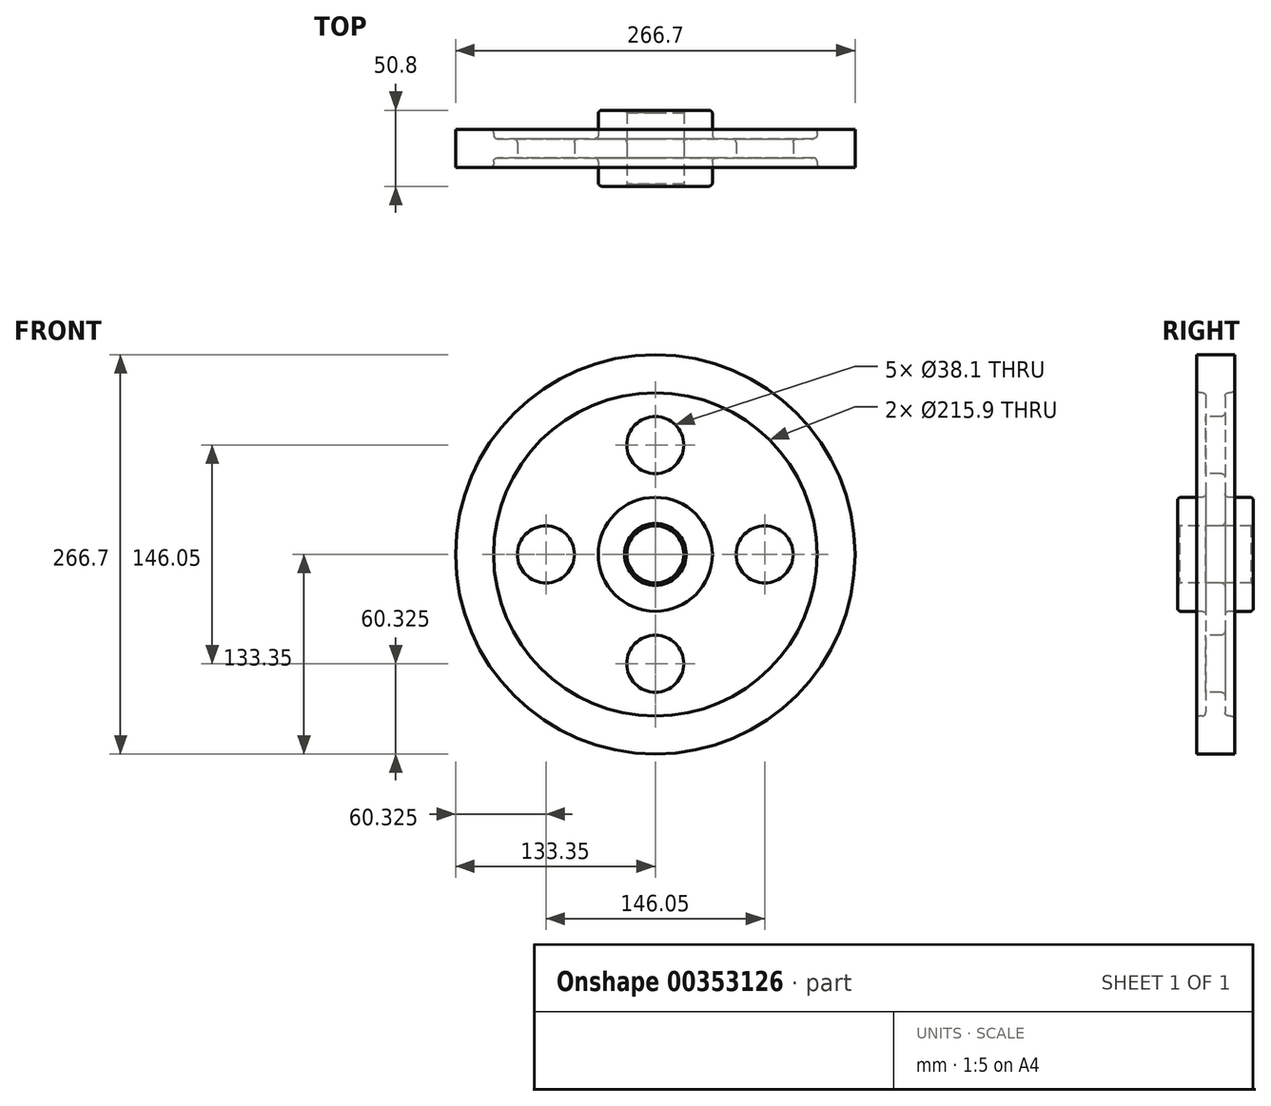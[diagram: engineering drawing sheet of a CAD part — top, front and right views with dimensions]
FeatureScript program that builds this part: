
annotation { "Feature Type Name" : "Feature", "Feature Type Description" : "" }
export const myFeature = defineFeature(function(context is Context, id is Id, definition is map)
    precondition{}
    {
        {
            var Q0;
            Q0=qCreatedBy(makeId("Right.planeOp"),FACE);
            var sketch = newSketch(context, id + "F0", { "sketchPlane" : qUnion([Q0])});
            skLineSegment(sketch, "E0", {"start": v(0, 0) * mm, "end": v(127.4, 0) * mm, "construction": true});
            skLineSegment(sketch, "E1.0", {"start": v(0, 19.05) * mm, "end": v(25.4, 19.05) * mm});
            skLineSegment(sketch, "E2.0", {"start": v(6.35, 38.1) * mm, "end": v(25.4, 38.1) * mm});
            skLineSegment(sketch, "E3.0", {"start": v(6.35, 107.95) * mm, "end": v(12.7, 107.95) * mm});
            skLineSegment(sketch, "E4.0", {"start": v(0, 133.35) * mm, "end": v(12.7, 133.35) * mm});
            skLineSegment(sketch, "E5", {"start": v(0, 133.35) * mm, "end": v(0, 0) * mm, "construction": true});
            skLineSegment(sketch, "E6.0", {"start": v(6.35, 107.95) * mm, "end": v(6.35, 38.1) * mm});
            skLineSegment(sketch, "E7.0", {"start": v(12.7, 133.35) * mm, "end": v(12.7, 107.95) * mm});
            skLineSegment(sketch, "E8.trimOffspring", {"start": v(25.4, 38.1) * mm, "end": v(25.4, 19.05) * mm});
            skLineSegment(sketch, "E9.MirrorCS", {"start": v(-6.35, 107.95) * mm, "end": v(-12.7, 107.95) * mm});
            skLineSegment(sketch, "E10.MirrorCS", {"start": v(-12.7, 133.35) * mm, "end": v(-12.7, 107.95) * mm});
            skLineSegment(sketch, "E11.MirrorCS", {"start": v(0, 133.35) * mm, "end": v(-12.7, 133.35) * mm});
            skLineSegment(sketch, "E12.MirrorCS", {"start": v(-6.35, 107.95) * mm, "end": v(-6.35, 38.1) * mm});
            skLineSegment(sketch, "E13.MirrorCS", {"start": v(-6.35, 38.1) * mm, "end": v(-25.4, 38.1) * mm});
            skLineSegment(sketch, "E14.MirrorCS", {"start": v(-25.4, 38.1) * mm, "end": v(-25.4, 19.05) * mm});
            skLineSegment(sketch, "E15.MirrorCS", {"start": v(0, 19.05) * mm, "end": v(-25.4, 19.05) * mm});
            skSolve(sketch);
        }
        {
            var Q0;
            Q0=makeQuery(id+"F0.imprint","IMPRINT",FACE,{"disambiguationData":[TD([[makeQuery(id+"F0.imprint","IMPRINT",EDGE,{"derivedFrom":sQuery(id+"F0.wireOp",EDGE,"E1.0")}),1.0]])]});
            var Q1;
            Q1=sQuery(id+"F0.wireOp",EDGE,"E0");
            revolve(context, id + "F1", {"entities" : qUnion([Q0]), "axis" : qUnion([Q1]), "revolveType" : RevolveType.FULL});
        }
        {
            var Q0;
            Q0=makeQuery(id+"F1.opRevolve","SWEPT_FACE",FACE,{"disambiguationData":[OSD([sQuery(id+"F0.wireOp",EDGE,"E12.MirrorCS")])]});
            var sketch = newSketch(context, id + "F2", { "sketchPlane" : qUnion([Q0])});
            skLineSegment(sketch, "E16", {"start": v(0, 0) * mm, "end": v(0, 73.03) * mm});
            skCircle(sketch, "E17", {"center": v(0, 73.03) * mm, "radius": 19.05 * mm});
            skCircle(sketch, "E18.1.0", {"center": v(-73.03, 0) * mm, "radius": 19.05 * mm});
            skCircle(sketch, "E18.2.0", {"center": v(0, -73.03) * mm, "radius": 19.05 * mm});
            skPoint(sketch, "E18.center", {"position": v(0, 0) * mm});
            skCircle(sketch, "E19.1.3.0", {"center": v(73.03, 0) * mm, "radius": 19.05 * mm});
            skSolve(sketch);
        }
        {
            var Q0;
            Q0=makeQuery(id+"F2.imprint","IMPRINT",FACE,{"disambiguationData":[TD([[makeQuery(id+"F2.imprint","IMPRINT",EDGE,{"derivedFrom":sQuery(id+"F2.wireOp",EDGE,"E17")}),1.0]])]});
            var Q1;
            Q1=makeQuery(id+"F2.imprint","IMPRINT",FACE,{"disambiguationData":[TD([[makeQuery(id+"F2.imprint","IMPRINT",EDGE,{"derivedFrom":sQuery(id+"F2.wireOp",EDGE,"E19.1.3.0")}),1.0]])]});
            var Q2;
            Q2=makeQuery(id+"F2.imprint","IMPRINT",FACE,{"disambiguationData":[TD([[makeQuery(id+"F2.imprint","IMPRINT",EDGE,{"derivedFrom":sQuery(id+"F2.wireOp",EDGE,"E18.2.0")}),1.0]])]});
            var Q3;
            Q3=makeQuery(id+"F2.imprint","IMPRINT",FACE,{"disambiguationData":[TD([[makeQuery(id+"F2.imprint","IMPRINT",EDGE,{"derivedFrom":sQuery(id+"F2.wireOp",EDGE,"E18.1.0")}),1.0]])]});
            extrude(context, id + "F3", {"entities" : qUnion([Q0, Q1, Q2, Q3]), "operationType" : NewBodyOperationType.REMOVE, "oppositeDirection" : true, "depth" : 25.4 * mm});
        }
        {
            var Q0;
            Q0=makeQuery(id+"F1.opRevolve","SWEPT_EDGE",EDGE,{"disambiguationData":[OSD([sQuery(id+"F0.wireOp",EDGE,"E9.MirrorCS"),sQuery(id+"F0.wireOp",EDGE,"E10.MirrorCS")])]});
            var Q1;
            Q1=makeQuery(id+"F1.opRevolve","SWEPT_EDGE",EDGE,{"disambiguationData":[OSD([sQuery(id+"F0.wireOp",EDGE,"E9.MirrorCS"),sQuery(id+"F0.wireOp",EDGE,"E12.MirrorCS")])]});
            var Q2;
            Q2=makeQuery(id+"F1.opRevolve","SWEPT_EDGE",EDGE,{"disambiguationData":[OSD([sQuery(id+"F0.wireOp",EDGE,"E12.MirrorCS"),sQuery(id+"F0.wireOp",EDGE,"E13.MirrorCS")])]});
            var Q3;
            Q3=makeQuery(id+"F1.opRevolve","SWEPT_EDGE",EDGE,{"disambiguationData":[OSD([sQuery(id+"F0.wireOp",EDGE,"E13.MirrorCS"),sQuery(id+"F0.wireOp",EDGE,"E14.MirrorCS")])]});
            var Q4;
            Q4=makeQuery(id+"F1.opRevolve","SWEPT_EDGE",EDGE,{"disambiguationData":[OSD([sQuery(id+"F0.wireOp",EDGE,"E3.0"),sQuery(id+"F0.wireOp",EDGE,"E7.0")])]});
            var Q5;
            Q5=makeQuery(id+"F1.opRevolve","SWEPT_FACE",FACE,{"disambiguationData":[OSD([sQuery(id+"F0.wireOp",EDGE,"E6.0")])]});
            var Q6;
            Q6=makeQuery(id+"F1.opRevolve","SWEPT_EDGE",EDGE,{"disambiguationData":[OSD([sQuery(id+"F0.wireOp",EDGE,"E2.0"),sQuery(id+"F0.wireOp",EDGE,"E8.trimOffspring")])]});
            var Q7;
            Q7=makeQuery(id+"F1.opRevolve","SWEPT_EDGE",EDGE,{"disambiguationData":[OSD([sQuery(id+"F0.wireOp",EDGE,"E2.0"),sQuery(id+"F0.wireOp",EDGE,"E6.0")])]});
            fillet(context, id + "F4", {"entities" : qUnion([Q0, Q1, Q2, Q3, Q4, Q5, Q6, Q7]), "radius" : 2.54 * mm, "tangentPropagation" : true, "allowEdgeOverflow" : false});
        }
        {
            var Q0;
            Q0=makeQuery(id+"F1.opRevolve","SWEPT_EDGE",EDGE,{"disambiguationData":[OSD([sQuery(id+"F0.wireOp",EDGE,"E1.0"),sQuery(id+"F0.wireOp",EDGE,"E8.trimOffspring")])]});
            var Q1;
            Q1=makeQuery(id+"F1.opRevolve","SWEPT_EDGE",EDGE,{"disambiguationData":[OSD([sQuery(id+"F0.wireOp",EDGE,"E14.MirrorCS"),sQuery(id+"F0.wireOp",EDGE,"E15.MirrorCS")])]});
            chamfer(context, id + "F5", {"entities" : qUnion([Q0, Q1]), "width" : 1.59 * mm, "tangentPropagation" : true});
        }
    });
